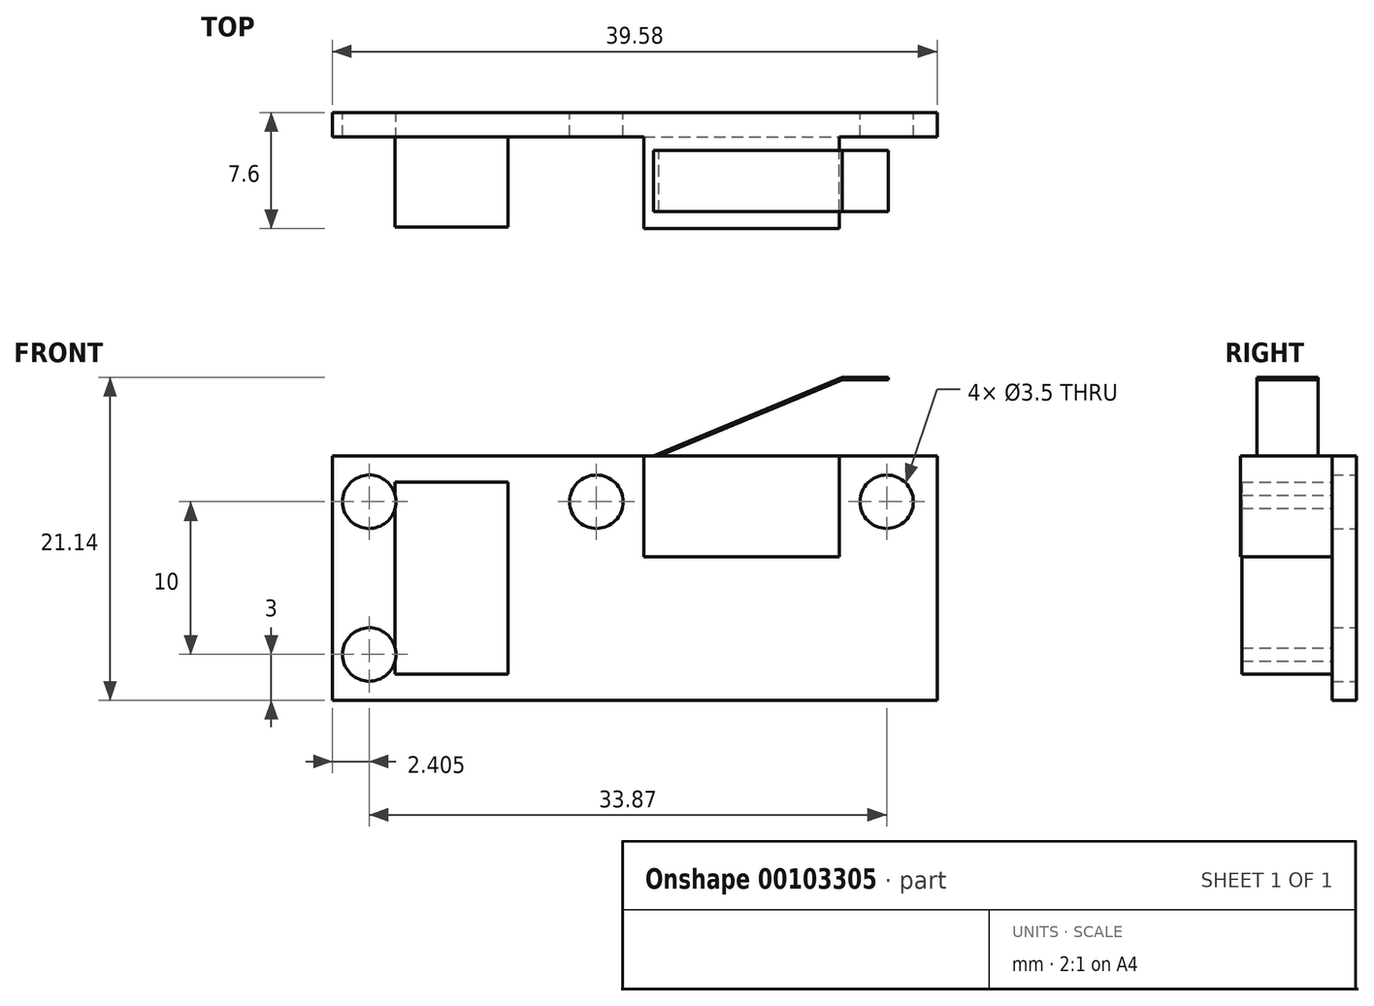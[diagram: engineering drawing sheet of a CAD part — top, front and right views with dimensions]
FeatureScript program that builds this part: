
annotation { "Feature Type Name" : "Feature", "Feature Type Description" : "" }
export const myFeature = defineFeature(function(context is Context, id is Id, definition is map)
    precondition{}
    {
        {
            var Q0;
            Q0=qCreatedBy(makeId("Front.planeOp"),FACE);
            var sketch = newSketch(context, id + "F0", { "sketchPlane" : qUnion([Q0])});
            skLineSegment(sketch, "E0.bottom", {"start": v(19.79, 8) * mm, "end": v(-19.79, 8) * mm});
            skLineSegment(sketch, "E0.top", {"start": v(19.79, -8) * mm, "end": v(-19.79, -8) * mm});
            skLineSegment(sketch, "E0.left", {"start": v(19.79, 8) * mm, "end": v(19.79, -8) * mm});
            skLineSegment(sketch, "E0.right", {"start": v(-19.79, 8) * mm, "end": v(-19.79, -8) * mm});
            skPoint(sketch, "E0.middle", {"position": v(0, 0) * mm});
            skLineSegment(sketch, "E1", {"start": v(-22.82, 5) * mm, "end": v(23.99, 5) * mm, "construction": true});
            skLineSegment(sketch, "E2", {"start": v(16.48, 11.4) * mm, "end": v(16.48, -14.56) * mm, "construction": true});
            skLineSegment(sketch, "E3", {"start": v(-2.52, 12.34) * mm, "end": v(-2.51, -14.75) * mm, "construction": true});
            skCircle(sketch, "E4", {"center": v(16.48, 5) * mm, "radius": 1.75 * mm});
            skCircle(sketch, "E5", {"center": v(-2.52, 5) * mm, "radius": 1.75 * mm});
            skLineSegment(sketch, "E6", {"start": v(-17.39, 11.6) * mm, "end": v(-17.39, -14.56) * mm, "construction": true});
            skCircle(sketch, "E7", {"center": v(-17.39, 5) * mm, "radius": 1.75 * mm});
            skLineSegment(sketch, "E8", {"start": v(-23.75, -5) * mm, "end": v(25.23, -5) * mm, "construction": true});
            skCircle(sketch, "E9", {"center": v(-17.39, -5) * mm, "radius": 1.75 * mm});
            skPoint(sketch, "E10.firstSnap0", {"position": v(0.59, 5) * mm});
            skLineSegment(sketch, "E10.bottom", {"start": v(0.59, 1.4) * mm, "end": v(13.39, 1.4) * mm});
            skLineSegment(sketch, "E10.top", {"start": v(0.58, 8) * mm, "end": v(13.38, 8) * mm});
            skLineSegment(sketch, "E10.left", {"start": v(0.59, 1.4) * mm, "end": v(0.58, 8) * mm});
            skLineSegment(sketch, "E10.right", {"start": v(13.39, 1.4) * mm, "end": v(13.38, 8) * mm});
            skLineSegment(sketch, "E11.bottom", {"start": v(-8.29, 6.3) * mm, "end": v(-15.69, 6.3) * mm});
            skLineSegment(sketch, "E11.top", {"start": v(-8.29, -6.3) * mm, "end": v(-15.69, -6.3) * mm});
            skLineSegment(sketch, "E11.left", {"start": v(-8.29, 6.3) * mm, "end": v(-8.29, -6.3) * mm});
            skLineSegment(sketch, "E11.right", {"start": v(-15.69, 6.3) * mm, "end": v(-15.69, -6.3) * mm});
            skPoint(sketch, "E12", {"position": v(-15.69, 0) * mm});
            skLineSegment(sketch, "E13", {"start": v(1.59, 8) * mm, "end": v(13.58, 13) * mm});
            skLineSegment(sketch, "E14", {"start": v(13.58, 13) * mm, "end": v(16.58, 13) * mm});
            skLineSegment(sketch, "E15", {"start": v(1.24, 8) * mm, "end": v(13.58, 13.14) * mm});
            skLineSegment(sketch, "E16", {"start": v(13.58, 13.14) * mm, "end": v(16.58, 13.14) * mm});
            skLineSegment(sketch, "E17", {"start": v(16.58, 13.14) * mm, "end": v(16.58, 13) * mm});
            skSolve(sketch);
        }
        {
            var Q0;
            Q0=makeQuery(id+"F0.imprint","IMPRINT",FACE,{"disambiguationData":[TD([[makeQuery(id+"F0.imprint","IMPRINT",EDGE,{"derivedFrom":sQuery(id+"F0.wireOp",EDGE,"E0.top")}),-1.0]])]});
            extrude(context, id + "F1", {"entities" : qUnion([Q0]), "depth" : 1.6 * mm});
        }
        {
            var Q0;
            Q0=makeQuery(id+"F0.imprint","IMPRINT",FACE,{"disambiguationData":[TD([[makeQuery(id+"F0.imprint","IMPRINT",EDGE,{"derivedFrom":sQuery(id+"F0.wireOp",EDGE,"E10.bottom")}),1.0]])]});
            extrude(context, id + "F2", {"entities" : qUnion([Q0]), "operationType" : NewBodyOperationType.ADD, "depth" : 7.6 * mm});
        }
        {
            var Q0;
            {var subQ1=sQuery(id+"F0.wireOp",EDGE,"E11.bottom");Q0=makeQuery(id+"F0.imprint","IMPRINT",FACE,{"disambiguationData":[TD([[makeQuery(id+"F0.imprint","IMPRINT",EDGE,{"derivedFrom":subQ1}),1.0]])]});}
            extrude(context, id + "F3", {"entities" : qUnion([Q0]), "operationType" : NewBodyOperationType.ADD, "depth" : 7.5 * mm});
        }
        {
            var Q0;
            {var subQ0=sQuery(id+"F0.wireOp",EDGE,"E13");Q0=makeQuery(id+"F0.imprint","IMPRINT",FACE,{"disambiguationData":[TD([[makeQuery(id+"F0.imprint","IMPRINT",EDGE,{"derivedFrom":subQ0}),1.0]])]});}
            extrude(context, id + "F4", {"entities" : qUnion([Q0]), "operationType" : NewBodyOperationType.ADD, "depth" : 6.5 * mm, "hasSecondDirection" : true, "secondDirectionOppositeDirection" : false, "secondDirectionDepth" : 2.5 * mm});
        }
    });
